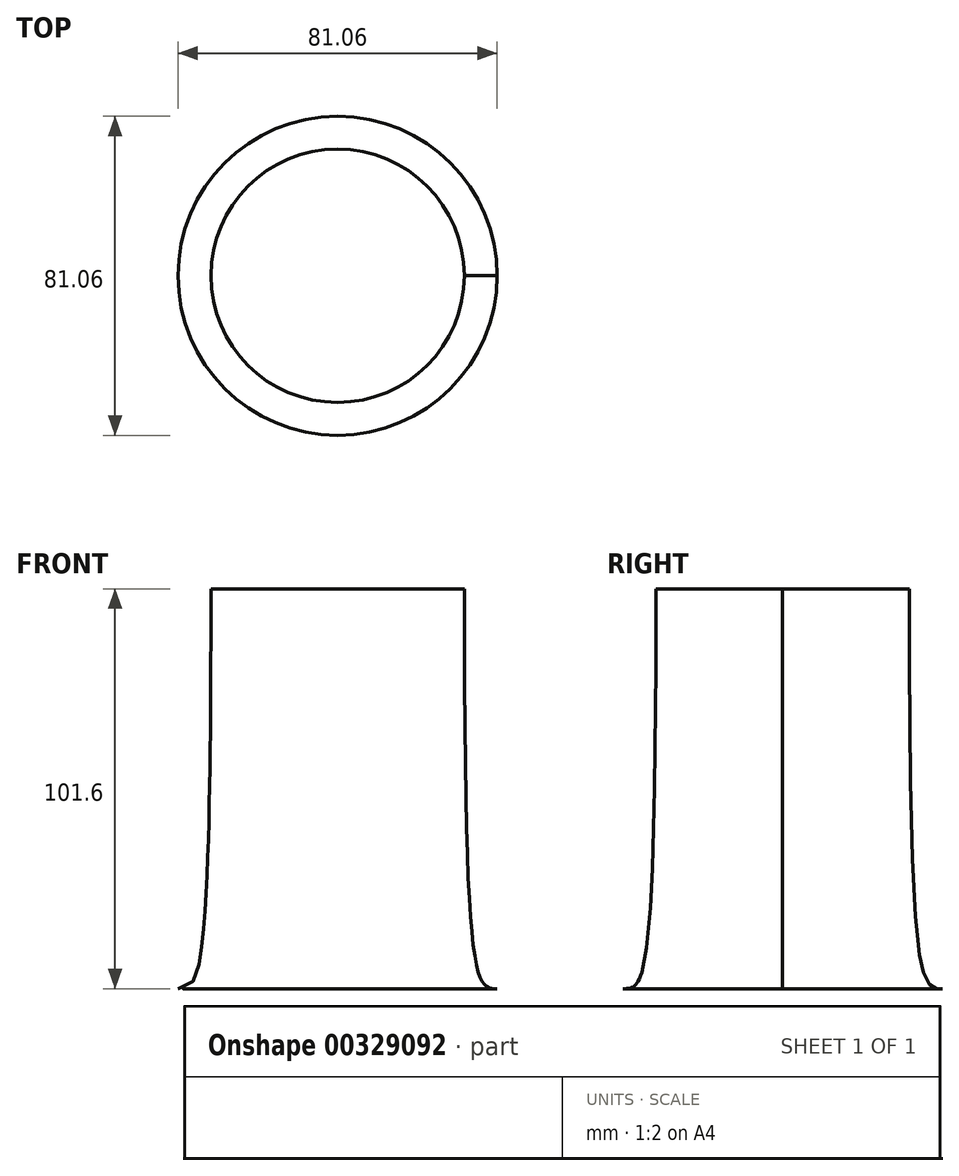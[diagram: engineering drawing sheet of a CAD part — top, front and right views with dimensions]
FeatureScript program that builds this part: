
annotation { "Feature Type Name" : "Feature", "Feature Type Description" : "" }
export const myFeature = defineFeature(function(context is Context, id is Id, definition is map)
    precondition{}
    {
        {
            var Q0;
            Q0=qCreatedBy(makeId("Top.planeOp"),FACE);
            var sketch = newSketch(context, id + "F0", { "sketchPlane" : qUnion([Q0])});
            skCircle(sketch, "E0", {"center": v(0, 0) * mm, "radius": 40.53 * mm});
            skSolve(sketch);
        }
        {
            var Q0;
            Q0=qCreatedBy(makeId("Top.planeOp"),FACE);
            cPlane(context, id + "F1", {"entities" : qUnion([Q0]), "cplaneType" : CPlaneType.OFFSET, "offset" : 101.6 * mm, "width" : 152.4 * mm, "height" : 152.4 * mm});
        }
        {
            var Q0;
            Q0=qCreatedBy(id+"F1.planeOp",FACE);
            var sketch = newSketch(context, id + "F2", { "sketchPlane" : qUnion([Q0])});
            skCircle(sketch, "E1", {"center": v(0, 0) * mm, "radius": 32.18 * mm});
            skSolve(sketch);
        }
        {
            var Q0;
            Q0=makeQuery(id+"F0.imprint","IMPRINT",FACE,{"disambiguationData":[TD([[makeQuery(id+"F0.imprint","IMPRINT",EDGE,{"derivedFrom":sQuery(id+"F0.wireOp",EDGE,"E0")}),1.0]])]});
            var Q1;
            Q1=makeQuery(id+"F2.imprint","IMPRINT",FACE,{"disambiguationData":[TD([[makeQuery(id+"F2.imprint","IMPRINT",EDGE,{"derivedFrom":sQuery(id+"F2.wireOp",EDGE,"E1")}),1.0]])]});
            loft(context, id + "F3", {"startCondition" : LoftEndDerivativeType.TANGENT_TO_PROFILE, "startMagnitude" : 2, "endCondition" : LoftEndDerivativeType.NORMAL_TO_PROFILE, "endMagnitude" : 3, "sheetProfilesArray" : [{ "sheetProfileEntities" : qUnion([Q0]) }, { "sheetProfileEntities" : qUnion([Q1]) }]});
        }
    });
